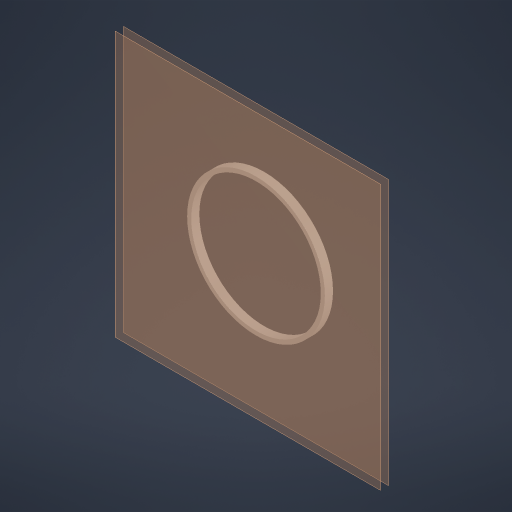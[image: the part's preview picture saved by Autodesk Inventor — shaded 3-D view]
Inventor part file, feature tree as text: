
AUTODESK INVENTOR PART (.ipt)
format: ipt  version: 2023.1 (Build 271208000, 208)  size: 174,592 bytes
history: native  units: mm
features: other x3, plane x2, extrude x1, sketch x1
ambient origin geometry x8: Origin, YZ Plane, XZ Plane, XY Plane, X Axis, Y Axis, Z Axis, Center Point
bodies: Solid1 (feature_tree)
feature tree (7):
  plane  "Work Plane1"
  plane  "Work Plane2"
  extrude  "Extrusion1"  Depth=10.0mm
  sketch  "Sketch1"  dims[d0=159.155mm d1=5.0mm d2=10.0mm d3=0.0mm]
  parser-record x1  (decoder bookkeeping rows leaked as tree rows — omitted from the tree; the rows remain in map.json)
  other  "Beau4tClock.iam"
  other  "Clock:1"
note: 1 file-system path scrubbed to <path> (originals preserved in map.json)
